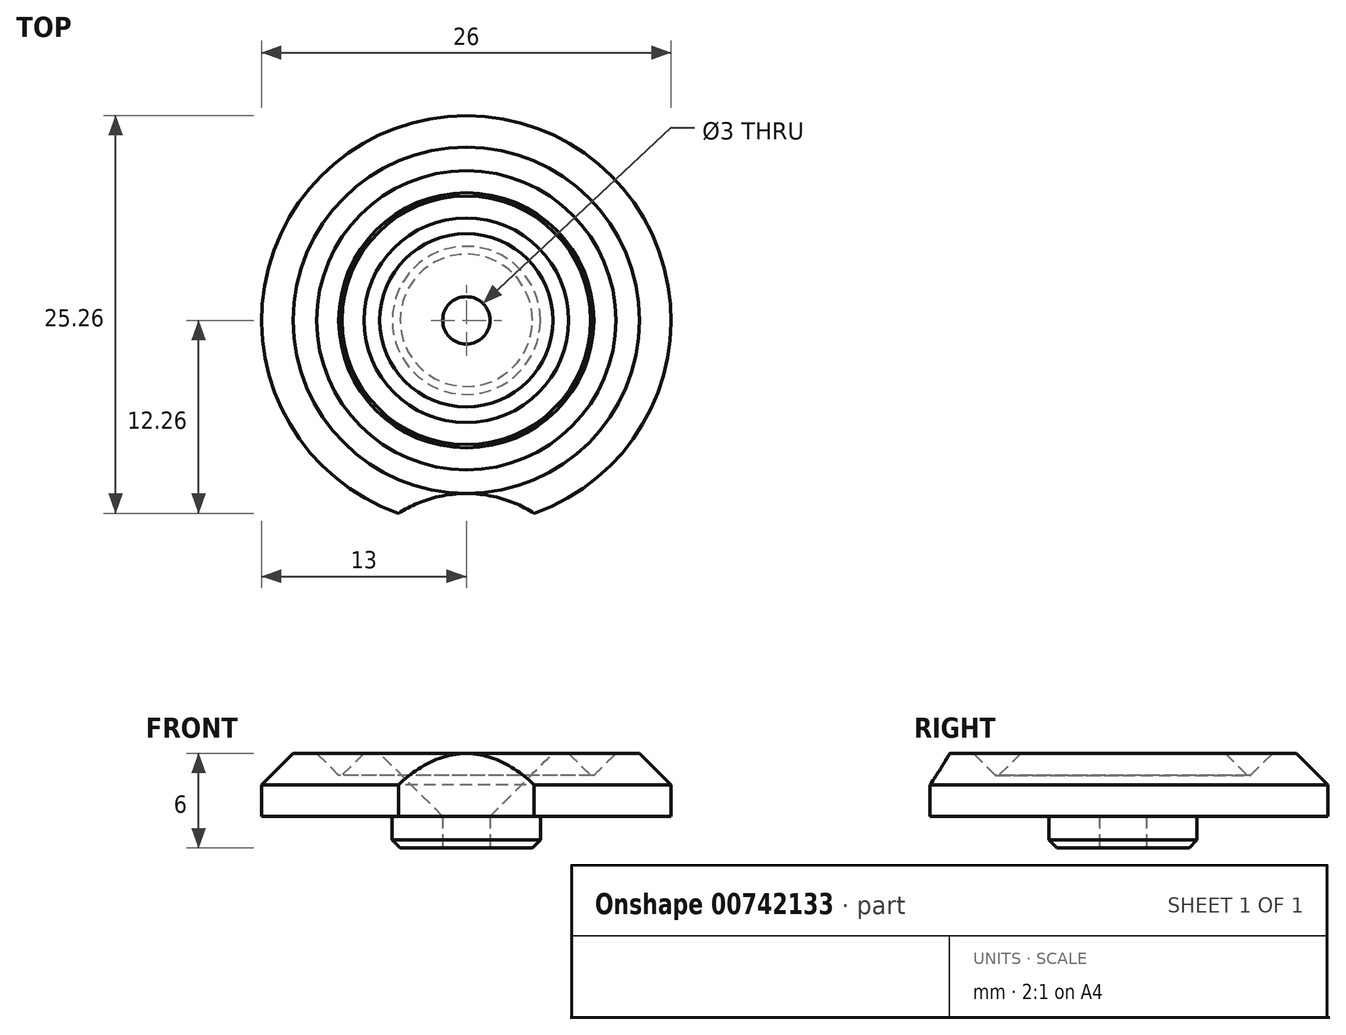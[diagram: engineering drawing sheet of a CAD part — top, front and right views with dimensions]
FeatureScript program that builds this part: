
annotation { "Feature Type Name" : "Feature", "Feature Type Description" : "" }
export const myFeature = defineFeature(function(context is Context, id is Id, definition is map)
    precondition{}
    {
        {
            var Q0;
            Q0=qCreatedBy(makeId("Top.planeOp"),FACE);
            var sketch = newSketch(context, id + "F0", { "sketchPlane" : qUnion([Q0])});
            skCircle(sketch, "E0", {"center": v(0, 0) * mm, "radius": 13 * mm});
            skLineSegment(sketch, "E1", {"start": v(0, 33.5) * mm, "end": v(0, -39.1) * mm, "construction": true});
            skLineSegment(sketch, "E2", {"start": v(30.36, 0) * mm, "end": v(-36.49, 0) * mm, "construction": true});
            skSolve(sketch);
        }
        {
            var Q0;
            Q0=qSketchRegion(id+"F0",true);
            extrude(context, id + "F1", {"entities" : qUnion([Q0]), "depth" : 4 * mm, "offsetDistance" : 25 * mm});
        }
        {
            var Q0;
            Q0=makeQuery(id+"F1.opExtrude","CAP_EDGE",EDGE,{"disambiguationData":[OSD([sQuery(id+"F0.wireOp",EDGE,"E0")])],"isStart":false});
            chamfer(context, id + "F2", {"entities" : qUnion([Q0]), "width" : 2 * mm, "tangentPropagation" : true});
        }
        {
            var Q0;
            Q0=makeQuery(id+"F1.opExtrude","CAP_FACE",FACE,{"disambiguationData":[OSD([sQuery(id+"F0.wireOp",EDGE,"E0")])],"isStart":true});
            var sketch = newSketch(context, id + "F3", { "sketchPlane" : qUnion([Q0])});
            skCircle(sketch, "E3", {"center": v(0, 0) * mm, "radius": 4.7 * mm});
            skSolve(sketch);
        }
        {
            var Q0;
            Q0=qSketchRegion(id+"F3",true);
            extrude(context, id + "F4", {"entities" : qUnion([Q0]), "operationType" : NewBodyOperationType.ADD, "depth" : 2 * mm, "offsetDistance" : 25 * mm});
        }
        {
            var Q0;
            Q0=makeQuery(id+"F4.opExtrude","CAP_EDGE",EDGE,{"disambiguationData":[OSD([sQuery(id+"F3.wireOp",EDGE,"E3")])],"isStart":false});
            chamfer(context, id + "F5", {"entities" : qUnion([Q0]), "width" : .5 * mm, "tangentPropagation" : true});
        }
        {
            var Q0;
            Q0=makeQuery(id+"F4.opExtrude","CAP_FACE",FACE,{"disambiguationData":[OSD([sQuery(id+"F3.wireOp",EDGE,"E3")])],"isStart":false});
            var sketch = newSketch(context, id + "F6", { "sketchPlane" : qUnion([Q0])});
            skCircle(sketch, "E4", {"center": v(0, 0) * mm, "radius": 1.5 * mm});
            skSolve(sketch);
        }
        {
            var Q0;
            Q0=qSketchRegion(id+"F6",true);
            extrude(context, id + "F7", {"entities" : qUnion([Q0]), "operationType" : NewBodyOperationType.REMOVE, "oppositeDirection" : true, "depth" : 25 * mm, "offsetDistance" : 25 * mm});
        }
        {
            var Q0;
            Q0=makeQuery(id+"F1.opExtrude","CAP_FACE",FACE,{"disambiguationData":[OSD([sQuery(id+"F0.wireOp",EDGE,"E0")])],"isStart":true});
            var sketch = newSketch(context, id + "F8", { "sketchPlane" : qUnion([Q0])});
            skLineSegment(sketch, "E5", {"start": v(0, 15.67) * mm, "end": v(0, -20.26) * mm, "construction": true});
            skCircle(sketch, "E6.0", {"center": v(0, 0) * mm, "radius": 13 * mm, "construction": true});
            skCircle(sketch, "E7", {"center": v(0, 19) * mm, "radius": 8 * mm});
            skSolve(sketch);
        }
        {
            var Q0;
            Q0=qSketchRegion(id+"F8",true);
            extrude(context, id + "F9", {"entities" : qUnion([Q0]), "operationType" : NewBodyOperationType.REMOVE, "oppositeDirection" : true, "depth" : 25 * mm, "offsetDistance" : 25 * mm});
        }
        {
            var Q0;
            Q0=makeQuery(id+"F1.opExtrude","CAP_FACE",FACE,{"disambiguationData":[OSD([sQuery(id+"F0.wireOp",EDGE,"E0")])],"isStart":false});
            var sketch = newSketch(context, id + "F10", { "sketchPlane" : qUnion([Q0])});
            skCircle(sketch, "E8", {"center": v(0, 0) * mm, "radius": 5 * mm});
            skCircle(sketch, "E9", {"center": v(0, 0) * mm, "radius": 6.5 * mm});
            skCircle(sketch, "E10", {"center": v(0, 0) * mm, "radius": 9.5 * mm});
            skSolve(sketch);
        }
        {
            var Q0;
            Q0=makeQuery(id+"F10.imprint","IMPRINT",FACE,{"disambiguationData":[TD([[makeQuery(id+"F10.imprint","IMPRINT",EDGE,{"derivedFrom":sQuery(id+"F10.wireOp",EDGE,"E9")}),-1.0]])]});
            extrude(context, id + "F11", {"entities" : qUnion([Q0]), "operationType" : NewBodyOperationType.REMOVE, "oppositeDirection" : true, "depth" : 1.4 * mm, "offsetDistance" : 25 * mm});
        }
        {
            var Q0;
            Q0=makeQuery(id+"F11.boolean.opBoolean","COPY",EDGE,{"derivedFrom":makeQuery(id+"F11.opExtrude","CAP_EDGE",EDGE,{"disambiguationData":[OSD([sQuery(id+"F10.wireOp",EDGE,"E10")])],"isStart":false})});
            var Q1;
            Q1=makeQuery(id+"F11.boolean.opBoolean","COPY",EDGE,{"derivedFrom":makeQuery(id+"F11.opExtrude","CAP_EDGE",EDGE,{"disambiguationData":[OSD([sQuery(id+"F10.wireOp",EDGE,"E9")])],"isStart":false})});
            chamfer(context, id + "F12", {"entities" : qUnion([Q0, Q1]), "width" : 1.4 * mm, "tangentPropagation" : true});
        }
        {
            var Q0;
            Q0=makeQuery(id+"F7.boolean.opBoolean","INTERSECT",EDGE,{"derivedFrom":[makeQuery(id+"F1.opExtrude","CAP_FACE",FACE,{"disambiguationData":[OSD([sQuery(id+"F0.wireOp",EDGE,"E0")])],"isStart":false}),makeQuery(id+"F7.opExtrude","SWEPT_FACE",FACE,{"disambiguationData":[OSD([sQuery(id+"F6.wireOp",EDGE,"E4")])]})]});
            chamfer(context, id + "F13", {"entities" : qUnion([Q0]), "width" : 4 * mm, "tangentPropagation" : true});
        }
    });
